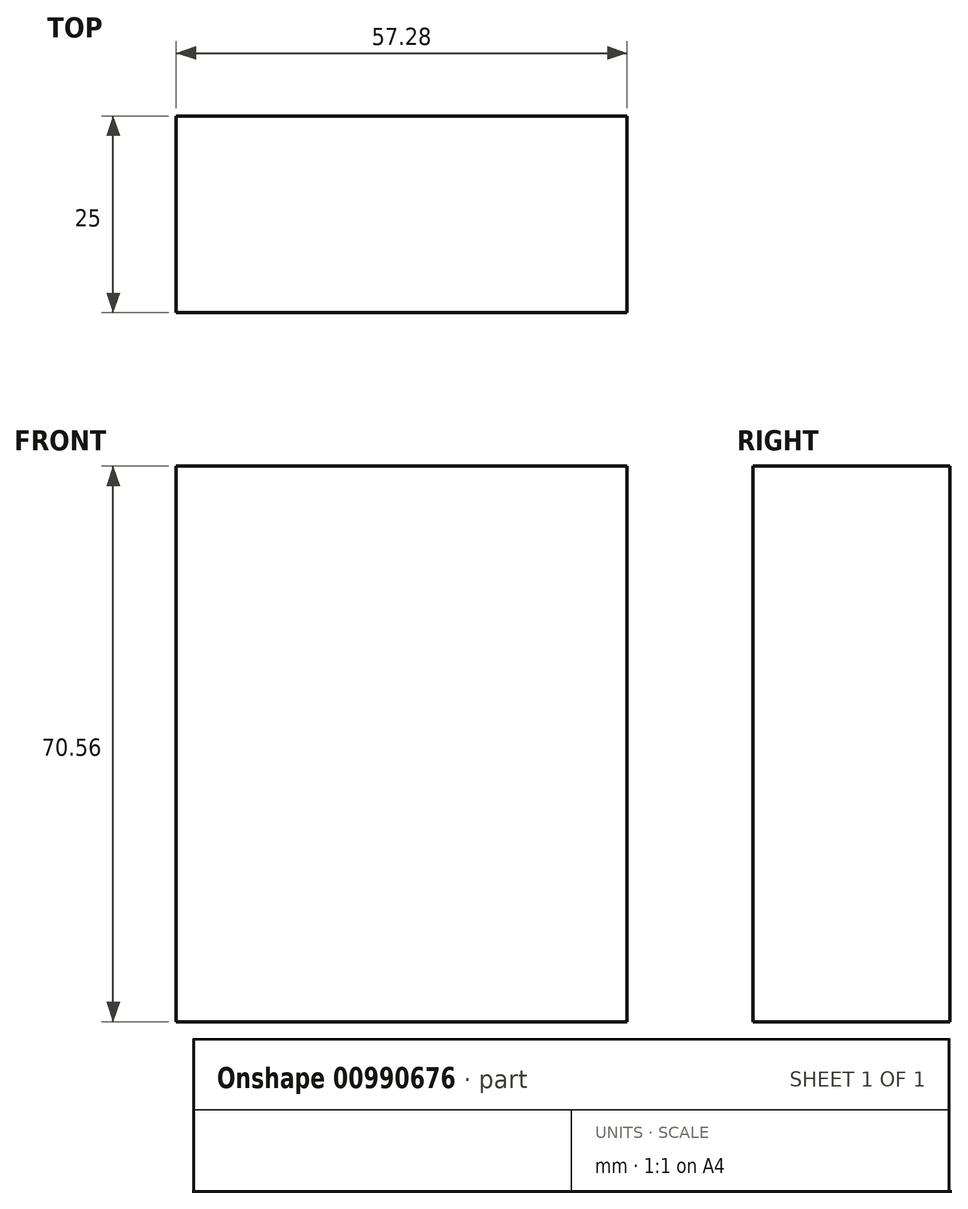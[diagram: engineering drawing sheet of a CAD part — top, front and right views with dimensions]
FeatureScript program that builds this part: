
annotation { "Feature Type Name" : "Feature", "Feature Type Description" : "" }
export const myFeature = defineFeature(function(context is Context, id is Id, definition is map)
    precondition{}
    {
        {
            var Q0;
            Q0=qCreatedBy(makeId("Front.planeOp"),FACE);
            var sketch = newSketch(context, id + "F0", { "sketchPlane" : qUnion([Q0])});
            skLineSegment(sketch, "E0.bottom", {"start": v(-124.35, 10.72) * mm, "end": v(-67.07, 10.72) * mm});
            skLineSegment(sketch, "E0.top", {"start": v(-124.35, -59.84) * mm, "end": v(-67.07, -59.84) * mm});
            skLineSegment(sketch, "E0.left", {"start": v(-124.35, 10.72) * mm, "end": v(-124.35, -59.84) * mm});
            skLineSegment(sketch, "E0.right", {"start": v(-67.07, 10.72) * mm, "end": v(-67.07, -59.84) * mm});
            skSolve(sketch);
        }
        {
            var Q0;
            Q0=qSketchRegion(id+"F0",true);
            extrude(context, id + "F1", {"entities" : qUnion([Q0]), "depth" : 25 * mm, "offsetDistance" : 25 * mm});
        }
    });
